# Revit family: Occupancy Detection Interface Unit _441
name_source: partatom
category: Electrical Fixtures
revit_build: Autodesk Revit 2018 (Build: 20170223_1515(x64)
units: mm (PartAtom-declared; Revit-internal decimal feet)

## family parameters
Always vertical = No
Cut with Voids When Loaded = No
Maintain Annotation Orientation = No
OmniClass Number = 23.80.00.00
OmniClass Title = Electric Power and Lighting
Part Type = Normal
Room Calculation Point = No
Round Connector Dimension = Use Diameter
Shared = No
Work Plane-Based = Yes

## types (1)
- Occupancy Detection Interface Unit
    Ambient temperature = 0 °C to +50 °C
    COLOUR MAPPING = 0V:Brown
T1:Red
T2:Orange
+12V:Yellow
0V:Green
DA+:Blue
DA-:Violet
    Connections: = 0 V input ground.
1 sensor input (normally closed).
2 for future use. Do not connect
    DALI consumption = 10 mA + sensor supply mA ≤ 25 mA max.
    DALI/switch/power = : Ribbon cable terminated with
7 ferrules
Ferrule pin ⌀ 1.2 mm
Note: To avoid interference
problems, the connections must
not be increased in length.
    Debounce period = 50 ms
    Default Elevation = 0 mm  [stored 0 ft]
    Designer: = 4.1 or later
    Dimensions: = 50 mm × 20 mm × 10 mm
    EMC emission = EN 55015
    EMC immunity = EN 61547
    Environment = Complies with WEEE and RoHS
directives.
    IP code: = IP20
    Manufacturer = Helvar
    Model = 441
    Overload protection = ± 7 V
    Relative humidity = Max. 90 %, noncondensing
    Safety = EN 60950
    Sensor supply = 12 V @ 15 mA max. (nonisolated)
0 V supply, common to input 0 V
    Short-circuit current = 1 mA max.
    Storage temperature = −10 °C to +70 °C
    Toolbox: = 2.2.12 or later
    Voltage at T1: = 5 V nominal with input open,
must be less than 1 V closed.
    Weight = 12 g

note: [stored X ft] marks values corroborated as IEEE doubles in the binary element streams (Revit-internal decimal feet)

## geometry (parser evidence)
native form markers: Sweep x3
no freeform markers — native parametric forms only
